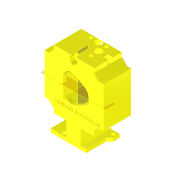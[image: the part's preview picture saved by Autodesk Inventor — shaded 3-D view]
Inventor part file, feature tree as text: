
AUTODESK INVENTOR PART (.ipt)
format: ipt  version: 2022 (Build 260153000, 153)  size: 846,848 bytes
history: native  units: mm
features: other x14, reference x12, sketch x9, extrude x8, projected_geometry x4, plane x3, chamfer x3, hole x2
ambient origin geometry x8: Origin, YZ Plane, XZ Plane, XY Plane, X Axis, Y Axis, Z Axis, Center Point
bodies: Solid1 (feature_tree)
feature tree (55):
  plane  "Work Plane1"
  extrude  "Extrusion1"  Depth=53.8mm
  extrude  "IM_offset"  Depth=53.8mm
  plane  "Arbeitsebene5"
  plane  "Arbeitsebene6"
  chamfer  "Fase2"  Distance=3.0mm
  extrude  "Extrusion27"  Depth=10.0mm
  other  "Arbeitsachse1"
  extrude  "Extrusion28"  Depth=10.0mm
  chamfer  "Fase3"  Distance=0.1mm
  extrude  "Extrusion29"  Depth=10.0mm
  extrude  "Extrusion30"  Depth=10.0mm
  extrude  "Extrusion32"  Depth=10.0mm TaperAngle=0.0deg
  extrude  "Extrusion33"  Depth=10.0mm TaperAngle=45.0deg
  chamfer  "Fase4"  Distance=1.0mm
  hole  "Bohrung2"  [1 undecoded]
  hole  "Bohrung3"  [1 undecoded]
  sketch  "Sketch1"  dims[d10=24.0mm d11=0.0mm d18=53.8mm]
  reference  "Reference1"
  reference  "Reference2"
  reference  "Reference3"
  reference  "Reference4"
  reference  "Reference9"
  reference  "Reference20"
  reference  "Reference21"
  reference  "Reference22"
  reference  "Reference23"
  reference  "Reference24"
  sketch  "Skizze4"  dims[d19=45.0deg d20=53.8mm]
  projected_geometry  "Projizierte Kontur1"
  sketch  "Skizze32"  dims[d21=45.0mm]
  projected_geometry  "Projizierte Kontur18"
  sketch  "Skizze34"  dims[d22=45.0mm]
  projected_geometry  "Projizierte Kontur19"
  sketch  "Skizze35"  dims[d30=20.0mm]
  reference  "Referenz34"
  reference  "Referenz35"
  sketch  "Skizze37"  dims[d31=20.0mm]
  sketch  "Skizze38"  dims[d32=2.8mm]
  projected_geometry  "Projizierte Kontur20"
  sketch  "Skizze39"  dims[d33=2.8mm]
  sketch  "Skizze40"  dims[d34=2.8mm d35=3.0mm d36=0.1mm d37=0.1mm d38=0.1mm d39=0.1mm d40=0.2mm d41=10.0mm d42=0.0mm d184=0.5mm d185=2.0mm d186=45.0deg d187=1.0mm d188=0.0mm d189=20.0mm d191=10.0mm d192=0.0mm d193=1.0mm d194=2.0mm d195=45.0deg d196=12.0mm d197=12.0mm d198=7.0mm d199=7.0mm d200=50.0mm d201=0.0mm d202=3.2mm d203=3.2mm d204=3.2mm d205=3.0mm d206=0.0mm d213=8.0mm d214=27.0mm d215=27.0mm d216=20.0mm d217=0.0mm d223=16.0mm d224=0.0mm d226=13.0mm d227=13.0mm d228=24.0mm d229=3.0mm d230=2.8mm d231=2.8mm d232=2.8mm d233=6.0mm d234=6.0mm d235=3.0mm d236=2.0mm d237=45.0deg d238=3.2mm d239=3.2mm d240=3.2mm d241=3.2mm d242=3.2mm d243=3.2mm d245=1.8mm d246=2.8mm d247=6.0mm d248=6.5mm d249=4.0mm d250=90.0deg d251=8.0mm d252=20.594885mm d253=2.8mm d254=2.8mm d255=6.0mm d256=6.5mm d257=4.0mm d258=90.0deg d259=8.0mm d260=20.594885mm d160=0.5mm d161=0.872665mm d162=0.5mm d163=0.872665mm]
  other  "Assembly_Cube_v2_Thorlabs.iam"
  other  "10_Cube_Base:1"
  other  "00_Base_v0:1"
  other  "Assembly_Cube_Kinematic_Mirrormount_v2.iam"
  other  "Assembly_Cube_empty_1x1_v2:1"
  other  "10_Cube_1x1_v2:1"
  other  "10_Lid_1x1_v2:1"
  other  "Assembly_Autofocus_ke400.iam"
  other  "00_KES_400_BlurayOPU:2"
  other  "00_KES400:1"
  other  "00_KES400_Bluray_Lens:1"
  other  "00_KES400A_base:1"
  other  "10_Cube_Lid:1"
note: 2 required parameter values undecoded (feature->parameter linkage not recoverable at this tier; creation-order binding heuristic only, values carry confidence <= 0.55)
